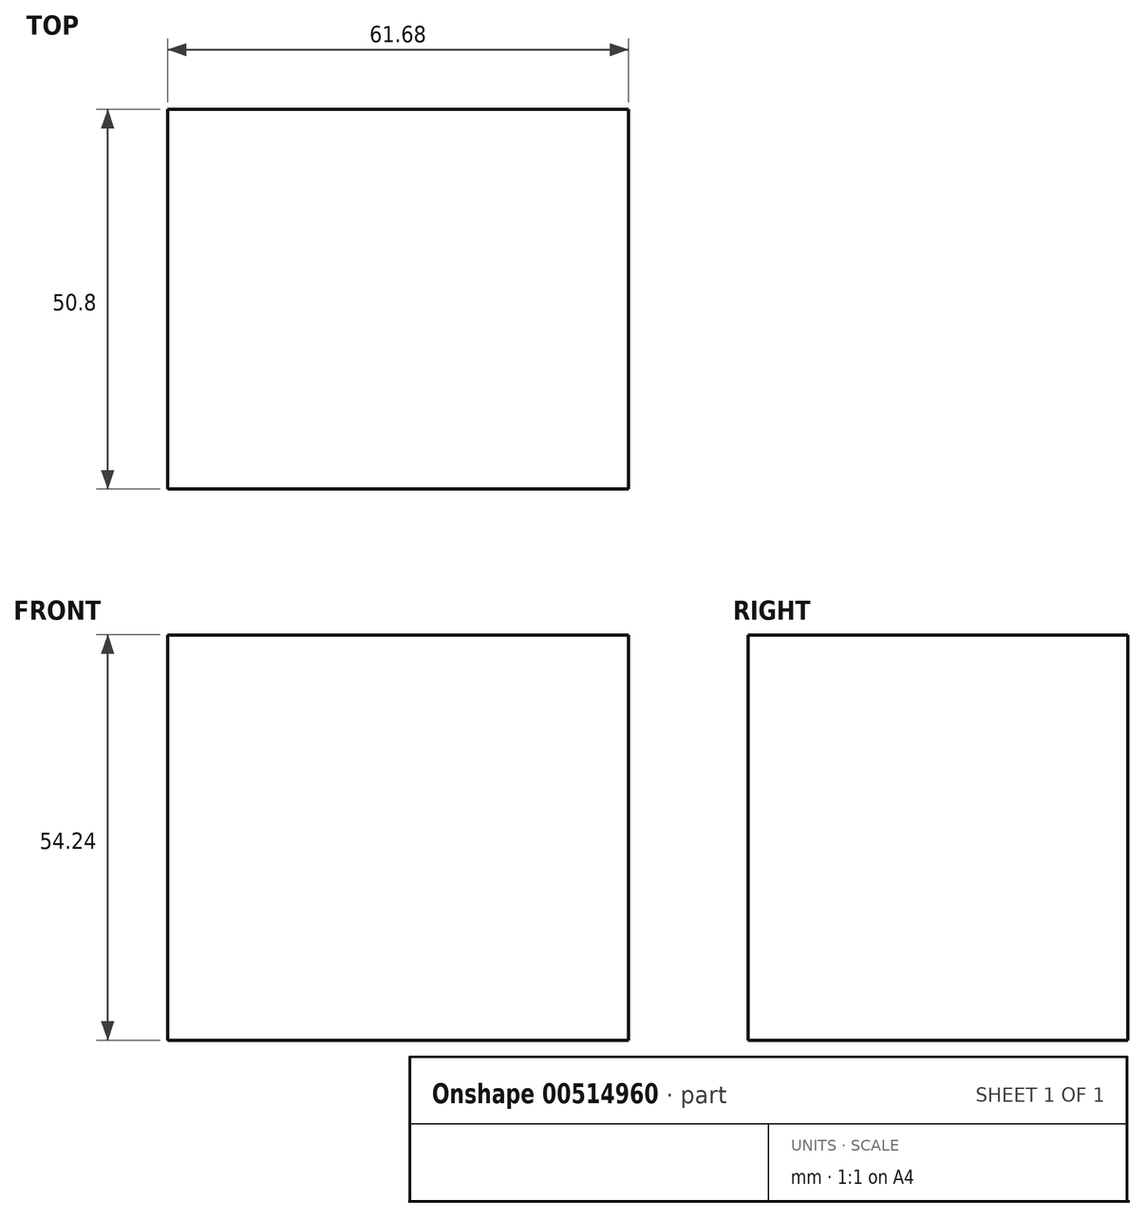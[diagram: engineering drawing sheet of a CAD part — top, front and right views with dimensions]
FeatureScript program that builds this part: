
annotation { "Feature Type Name" : "Feature", "Feature Type Description" : "" }
export const myFeature = defineFeature(function(context is Context, id is Id, definition is map)
    precondition{}
    {
        {
            var Q0;
            Q0=qCreatedBy(makeId("Front.planeOp"),FACE);
            var sketch = newSketch(context, id + "F0", { "sketchPlane" : qUnion([Q0])});
            skLineSegment(sketch, "E0.bottom", {"start": v(-47.17, 37.05) * mm, "end": v(14.51, 37.05) * mm});
            skLineSegment(sketch, "E0.top", {"start": v(-47.17, -17.19) * mm, "end": v(14.51, -17.19) * mm});
            skLineSegment(sketch, "E0.left", {"start": v(-47.17, 37.05) * mm, "end": v(-47.17, -17.19) * mm});
            skLineSegment(sketch, "E0.right", {"start": v(14.51, 37.05) * mm, "end": v(14.51, -17.19) * mm});
            skSolve(sketch);
        }
        {
            var Q0;
            Q0=makeQuery(id+"F0.imprint","IMPRINT",FACE,{"disambiguationData":[TD([[makeQuery(id+"F0.imprint","IMPRINT",EDGE,{"derivedFrom":sQuery(id+"F0.wireOp",EDGE,"E0.bottom")}),-1.0]])]});
            extrude(context, id + "F1", {"entities" : qUnion([Q0]), "depth" : 50.8 * mm, "offsetDistance" : 25.4 * mm});
        }
    });
